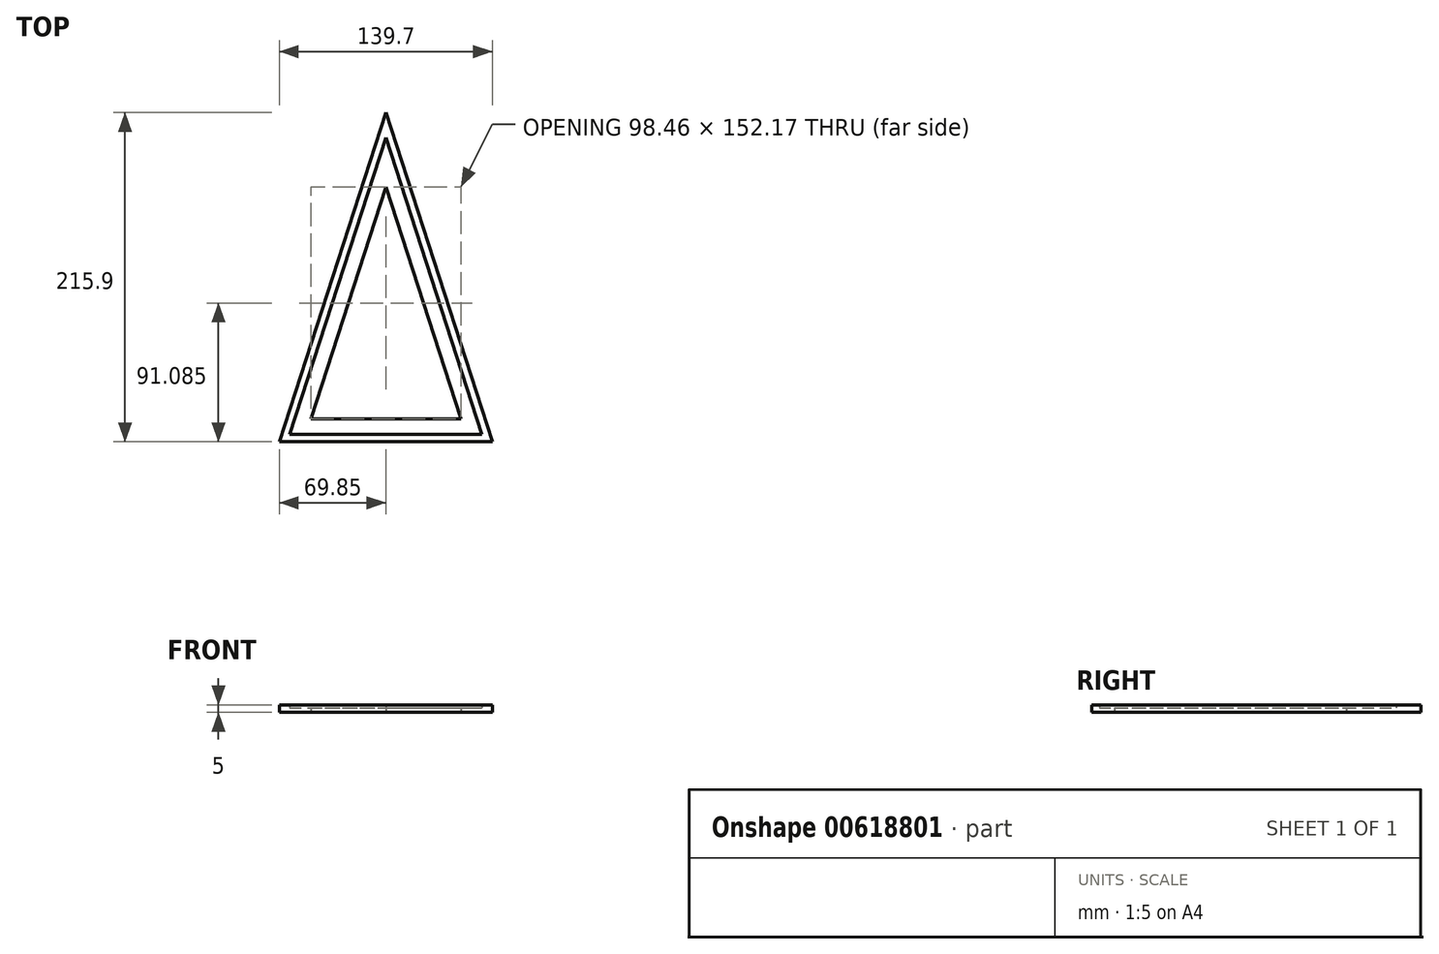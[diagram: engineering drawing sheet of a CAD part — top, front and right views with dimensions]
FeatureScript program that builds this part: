
annotation { "Feature Type Name" : "Feature", "Feature Type Description" : "" }
export const myFeature = defineFeature(function(context is Context, id is Id, definition is map)
    precondition{}
    {
        {
            var Q0;
            Q0=qCreatedBy(makeId("Top.planeOp"),FACE);
            var sketch = newSketch(context, id + "F0", { "sketchPlane" : qUnion([Q0])});
            skLineSegment(sketch, "E0.bottom", {"start": v(69.85, 107.95) * mm, "end": v(-69.85, 107.95) * mm, "construction": true});
            skLineSegment(sketch, "E0.top", {"start": v(69.85, -107.95) * mm, "end": v(-69.85, -107.95) * mm, "construction": true});
            skLineSegment(sketch, "E0.left", {"start": v(69.85, 107.95) * mm, "end": v(69.85, -107.95) * mm, "construction": true});
            skLineSegment(sketch, "E0.right", {"start": v(-69.85, 107.95) * mm, "end": v(-69.85, -107.95) * mm, "construction": true});
            skPoint(sketch, "E0.middle", {"position": v(0, 0) * mm});
            skLineSegment(sketch, "E1", {"start": v(0, 0) * mm, "end": v(0, 107.95) * mm, "construction": true});
            skLineSegment(sketch, "E2", {"start": v(-69.85, -107.95) * mm, "end": v(69.85, -107.95) * mm});
            skLineSegment(sketch, "E3", {"start": v(0, 107.95) * mm, "end": v(69.85, -107.95) * mm});
            skLineSegment(sketch, "E4", {"start": v(-69.85, -107.95) * mm, "end": v(0, 107.95) * mm});
            skLineSegment(sketch, "E5.0", {"start": v(-62.98, -102.95) * mm, "end": v(0, 91.7) * mm});
            skLineSegment(sketch, "E5.1", {"start": v(-62.98, -102.95) * mm, "end": v(62.98, -102.95) * mm});
            skLineSegment(sketch, "E5.2", {"start": v(0, 91.7) * mm, "end": v(62.98, -102.95) * mm});
            skLineSegment(sketch, "E6.0", {"start": v(0, 59.22) * mm, "end": v(49.23, -92.95) * mm});
            skLineSegment(sketch, "E6.1", {"start": v(-49.23, -92.95) * mm, "end": v(0, 59.22) * mm});
            skLineSegment(sketch, "E6.2", {"start": v(-49.23, -92.95) * mm, "end": v(49.23, -92.95) * mm});
            skSolve(sketch);
        }
        {
            var Q0;
            Q0=makeQuery(id+"F0.imprint","IMPRINT",FACE,{"disambiguationData":[TD([[makeQuery(id+"F0.imprint","IMPRINT",EDGE,{"derivedFrom":sQuery(id+"F0.wireOp",EDGE,"E2")}),1.0]])]});
            extrude(context, id + "F1", {"entities" : qUnion([Q0]), "depth" : 5 * mm, "offsetDistance" : 25 * mm});
        }
        {
            var Q0;
            Q0=makeQuery(id+"F0.imprint","IMPRINT",FACE,{"disambiguationData":[TD([[makeQuery(id+"F0.imprint","IMPRINT",EDGE,{"derivedFrom":sQuery(id+"F0.wireOp",EDGE,"E5.0")}),-1.0]])]});
            extrude(context, id + "F2", {"entities" : qUnion([Q0]), "operationType" : NewBodyOperationType.ADD, "depth" : 3 * mm, "offsetDistance" : 25 * mm});
        }
    });
